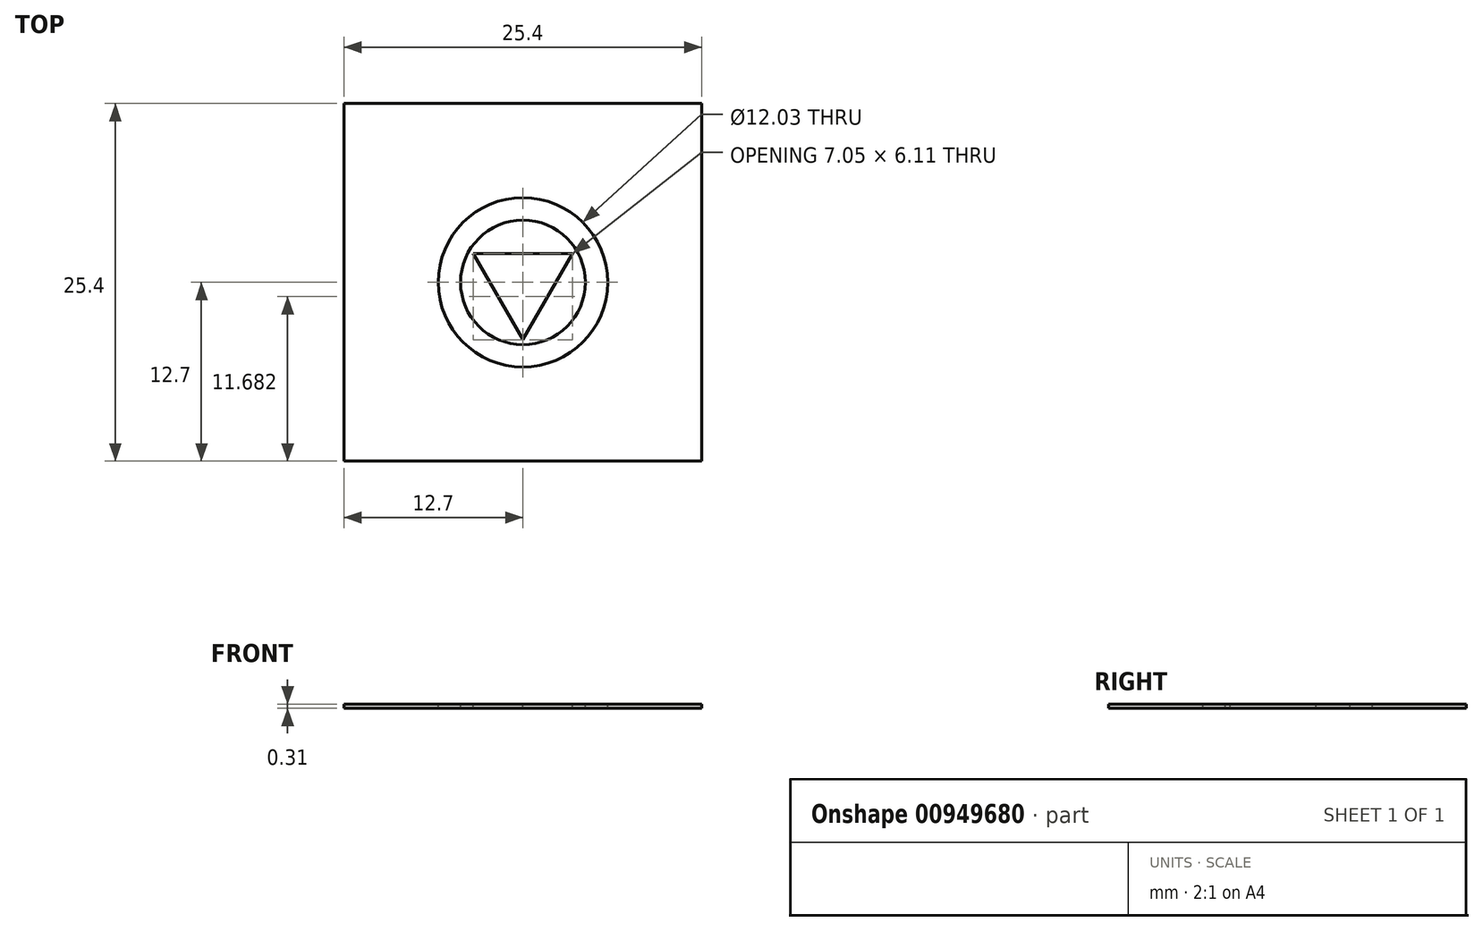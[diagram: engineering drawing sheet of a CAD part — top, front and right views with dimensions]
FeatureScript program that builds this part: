
annotation { "Feature Type Name" : "Feature", "Feature Type Description" : "" }
export const myFeature = defineFeature(function(context is Context, id is Id, definition is map)
    precondition{}
    {
        {
            var Q0;
            Q0=qCreatedBy(makeId("Top.planeOp"),FACE);
            var sketch = newSketch(context, id + "F0", { "sketchPlane" : qUnion([Q0])});
            skLineSegment(sketch, "E0.bottom", {"start": v(12.7, 12.7) * mm, "end": v(-12.7, 12.7) * mm});
            skLineSegment(sketch, "E0.top", {"start": v(12.7, -12.7) * mm, "end": v(-12.7, -12.7) * mm});
            skLineSegment(sketch, "E0.left", {"start": v(12.7, 12.7) * mm, "end": v(12.7, -12.7) * mm});
            skLineSegment(sketch, "E0.right", {"start": v(-12.7, 12.7) * mm, "end": v(-12.7, -12.7) * mm});
            skPoint(sketch, "E0.middle", {"position": v(0, 0) * mm});
            skCircle(sketch, "E1", {"center": v(0, 0) * mm, "radius": 1.59 * mm});
            skSolve(sketch);
        }
        {
            var Q0;
            Q0=makeQuery(id+"F0.imprint","IMPRINT",FACE,{"disambiguationData":[TD([[makeQuery(id+"F0.imprint","IMPRINT",EDGE,{"derivedFrom":sQuery(id+"F0.wireOp",EDGE,"E0.bottom")}),1.0]])]});
            extrude(context, id + "F1", {"entities" : qUnion([Q0]), "depth" : (.25 + (1 / 16)) * mm, "offsetDistance" : 25.4 * mm});
        }
        {
            var Q0;
            Q0=makeQuery(id+"F1.opExtrude","CAP_FACE",FACE,{"disambiguationData":[OSD([sQuery(id+"F0.wireOp",EDGE,"E0.bottom"),sQuery(id+"F0.wireOp",EDGE,"E0.top"),sQuery(id+"F0.wireOp",EDGE,"E0.left"),sQuery(id+"F0.wireOp",EDGE,"E0.right"),sQuery(id+"F0.wireOp",EDGE,"E1")])],"isStart":false});
            var sketch = newSketch(context, id + "F2", { "sketchPlane" : qUnion([Q0])});
            skCircle(sketch, "E2.cCircle", {"center": v(0, 0) * mm, "radius": 4.07 * mm, "construction": true});
            skLineSegment(sketch, "E2.0", {"start": v(0, -4.07) * mm, "end": v(-3.53, 2.04) * mm});
            skLineSegment(sketch, "E2.1", {"start": v(-3.53, 2.04) * mm, "end": v(3.53, 2.04) * mm});
            skLineSegment(sketch, "E2.2", {"start": v(3.53, 2.04) * mm, "end": v(0, -4.07) * mm});
            skSolve(sketch);
        }
        {
            var Q0;
            Q0 = qSketchRegion(id + "F2", true);
            extrude(context, id + "F3", {"entities" : qUnion([Q0]), "operationType" : NewBodyOperationType.REMOVE, "oppositeDirection" : true, "depth" : 6.35 * mm, "offsetDistance" : 25.4 * mm, "hasDraft" : true, "draftAngle" : .5 * degree, "draftPullDirection" : true});
        }
        {
            var Q0;
            Q0=qCreatedBy(makeId("Right.planeOp"),FACE);
            var sketch = newSketch(context, id + "F4", { "sketchPlane" : qUnion([Q0])});
            skLineSegment(sketch, "E3", {"start": v(-4.43, 7.94) * mm, "end": v(-4.43, 0) * mm});
            skLineSegment(sketch, "E4", {"start": v(-4.43, 0) * mm, "end": v(-6.01, 0) * mm});
            skLineSegment(sketch, "E5", {"start": v(-6.01, 0) * mm, "end": v(-6.01, 4.09) * mm});
            skLineSegment(sketch, "E6", {"start": v(-6.01, 4.09) * mm, "end": v(-8.24, 7.94) * mm});
            skLineSegment(sketch, "E7", {"start": v(-8.24, 7.94) * mm, "end": v(-4.43, 7.94) * mm});
            skLineSegment(sketch, "E8", {"start": v(-4.43, 0) * mm, "end": v(0, 0) * mm, "construction": true});
            skLineSegment(sketch, "E9", {"start": v(0, 0) * mm, "end": v(0, 7.94) * mm, "construction": true});
            skSolve(sketch);
        }
        {
            var Q0;
            Q0=makeQuery(id+"F4.imprint","IMPRINT",FACE,{"disambiguationData":[TD([[makeQuery(id+"F4.imprint","IMPRINT",EDGE,{"derivedFrom":sQuery(id+"F4.wireOp",EDGE,"E3")}),-1.0]])]});
            var Q1;
            Q1=sQuery(id+"F4.wireOp",EDGE,"E9");
            revolve(context, id + "F5", {"operationType" : NewBodyOperationType.REMOVE, "surfaceOperationType" : NewSurfaceOperationType.NEW, "entities" : qUnion([Q0]), "axis" : qUnion([Q1]), "revolveType" : RevolveType.FULL, "oppositeDirection" : true});
        }
    });
